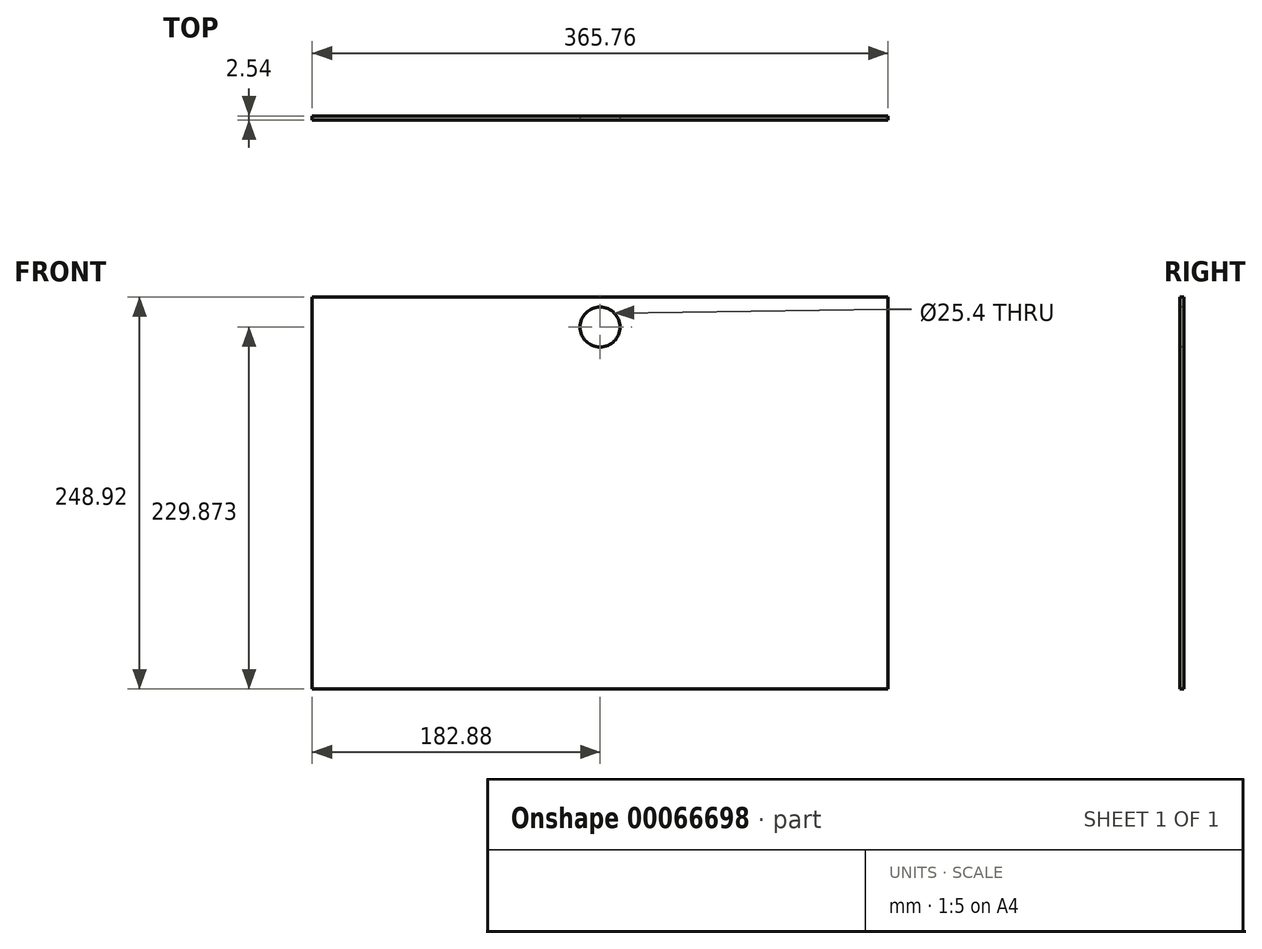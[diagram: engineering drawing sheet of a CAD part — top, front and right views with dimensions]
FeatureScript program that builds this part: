
annotation { "Feature Type Name" : "Feature", "Feature Type Description" : "" }
export const myFeature = defineFeature(function(context is Context, id is Id, definition is map)
    precondition{}
    {
        {
            var Q0;
            Q0=qCreatedBy(makeId("Front.planeOp"),FACE);
            var sketch = newSketch(context, id + "F0", { "sketchPlane" : qUnion([Q0])});
            skLineSegment(sketch, "E0.bottom", {"start": v(-182.88, 120.72) * mm, "end": v(182.88, 120.72) * mm});
            skLineSegment(sketch, "E0.top", {"start": v(-182.88, -128.2) * mm, "end": v(182.88, -128.2) * mm});
            skLineSegment(sketch, "E0.left", {"start": v(-182.88, 120.72) * mm, "end": v(-182.88, -128.2) * mm});
            skLineSegment(sketch, "E0.right", {"start": v(182.88, 120.72) * mm, "end": v(182.88, -128.2) * mm});
            skSolve(sketch);
        }
        {
            var Q0;
            Q0 = qSketchRegion(id + "F0", true);
            extrude(context, id + "F1", {"entities" : qUnion([Q0]), "depth" : 2.54 * mm});
        }
        {
            var Q0;
            Q0=makeQuery(id+"F1.opExtrude","CAP_FACE",FACE,{"disambiguationData":[OSD([sQuery(id+"F0.wireOp",EDGE,"E0.bottom"),sQuery(id+"F0.wireOp",EDGE,"E0.top"),sQuery(id+"F0.wireOp",EDGE,"E0.left"),sQuery(id+"F0.wireOp",EDGE,"E0.right")])],"isStart":false});
            var sketch = newSketch(context, id + "F2", { "sketchPlane" : qUnion([Q0])});
            skLineSegment(sketch, "E1.bottom", {"start": v(-12.7, 120.72) * mm, "end": v(12.7, 120.72) * mm, "construction": true});
            skLineSegment(sketch, "E1.top", {"start": v(-12.7, 82.62) * mm, "end": v(12.7, 82.62) * mm, "construction": true});
            skLineSegment(sketch, "E1.left", {"start": v(-12.7, 120.72) * mm, "end": v(-12.7, 82.62) * mm, "construction": true});
            skLineSegment(sketch, "E1.right", {"start": v(12.7, 120.72) * mm, "end": v(12.7, 82.62) * mm, "construction": true});
            skLineSegment(sketch, "E2", {"start": v(0, 120.72) * mm, "end": v(0, -128.2) * mm, "construction": true});
            skPoint(sketch, "E2.startSnap0", {"position": v(0, 120.72) * mm});
            skLineSegment(sketch, "E3", {"start": v(-42.58, 101.67) * mm, "end": v(43.13, 101.67) * mm, "construction": true});
            skCircle(sketch, "E4", {"center": v(0, 101.67) * mm, "radius": 12.7 * mm});
            skSolve(sketch);
        }
        {
            var Q0;
            Q0 = qSketchRegion(id + "F2", true);
            var Q1;
            Q1=sQuery(id+"F2.wireOp",EDGE,"E4");
            extrude(context, id + "F3", {"entities" : qUnion([Q0]), "operationType" : NewBodyOperationType.REMOVE, "surfaceEntities" : qUnion([Q1]), "oppositeDirection" : true, "depth" : 2.54 * mm});
        }
    });
